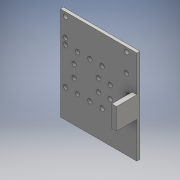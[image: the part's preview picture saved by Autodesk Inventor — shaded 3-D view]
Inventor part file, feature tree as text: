
AUTODESK INVENTOR PART (.ipt)
format: ipt  version: 2016 (Build 200138000, 138)  size: 173,056 bytes
history: native  units: mm
features: sketch x3, extrude x2, hole x1
ambient origin geometry x8: Origin, YZ Plane, XZ Plane, XY Plane, X Axis, Y Axis, Z Axis, Center Point
bodies: Solid1 (feature_tree)
feature tree (6):
  extrude  "Extrusion1"  Depth=92.0mm
  extrude  "Extrusion2"  Depth=18.0mm
  hole  "Hole1"  [1 undecoded]
  sketch  "Sketch1"  dims[d0=75.0mm d1=92.0mm]
  sketch  "Sketch3"  dims[d6=4.35mm d7=18.0mm]
  sketch  "Sketch5"  dims[d8=4.35mm d9=18.0mm d10=4.35mm d11=12.0mm d12=4.35mm d13=4.35mm d14=12.0mm d15=4.35mm d16=4.35mm d17=12.0mm d18=4.35mm d19=12.0mm d20=12.0mm d21=12.0mm d22=3.0mm d23=0.0mm d24=10.5mm d25=4.5mm d26=21.0mm d27=20.0mm d28=0.0mm d29=4.35mm d30=6.0mm d31=8.0mm d32=4.35mm d33=6.0mm d34=4.35mm d35=18.0mm d36=4.35mm d37=4.35mm d40=4.35mm d42=4.35mm d44=4.35mm d45=4.35mm d46=4.35mm d47=18.0mm d48=6.0mm d50=6.0mm d51=6.0mm d52=6.0mm d53=12.0mm d54=4.35mm d55=60.0mm d56=4.35mm d57=4.35mm d58=6.0mm d59=4.0mm d60=2.0mm d61=90.0deg d62=8.0mm d63=20.594885mm d64=24.0mm d65=24.0mm]
note: 1 required parameter value undecoded (feature->parameter linkage not recoverable at this tier; creation-order binding heuristic only, values carry confidence <= 0.55)
